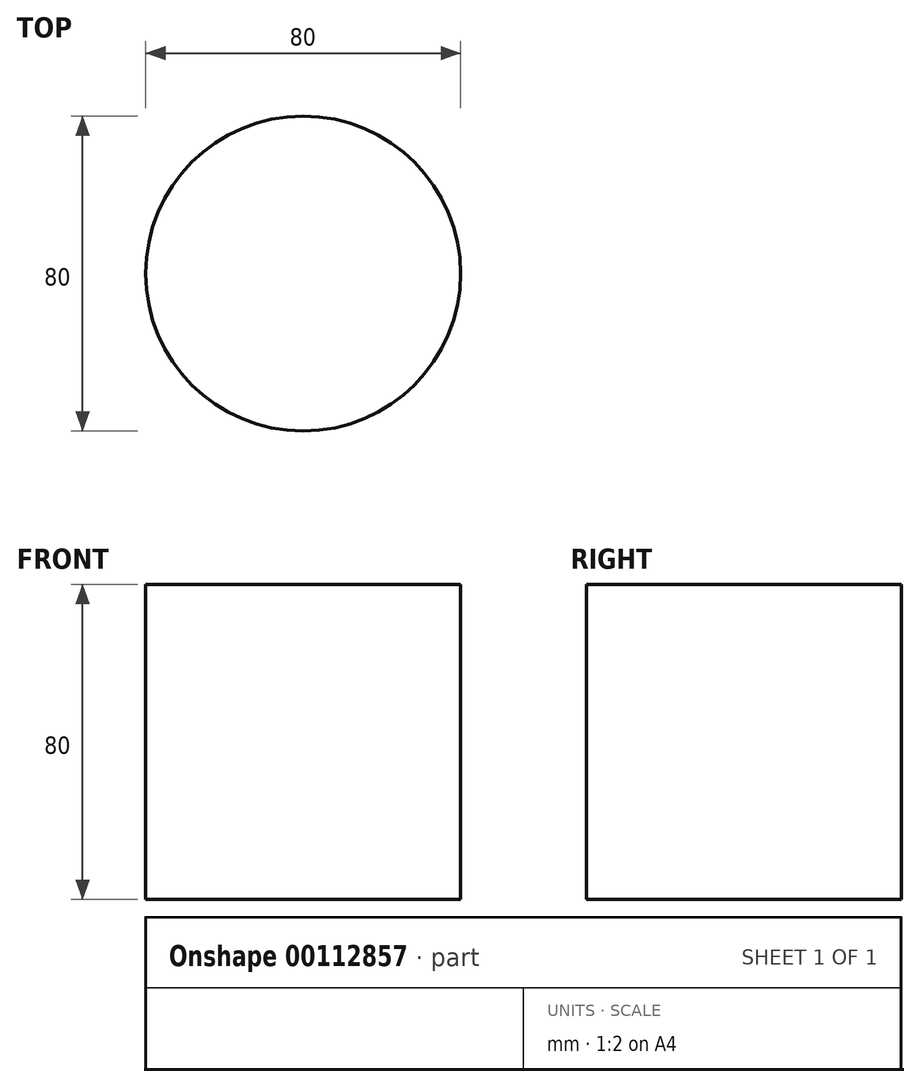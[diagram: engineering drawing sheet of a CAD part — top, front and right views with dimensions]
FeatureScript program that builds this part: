
annotation { "Feature Type Name" : "Feature", "Feature Type Description" : "" }
export const myFeature = defineFeature(function(context is Context, id is Id, definition is map)
    precondition{}
    {
        {
            var Q0;
            Q0=qCreatedBy(makeId("Top.planeOp"),FACE);
            var sketch = newSketch(context, id + "F0", { "sketchPlane" : qUnion([Q0])});
            skCircle(sketch, "E0", {"center": v(17.7, 0) * mm, "radius": 40 * mm});
            skSolve(sketch);
        }
        {
            var Q0;
            Q0=makeQuery(id+"F0.imprint","IMPRINT",FACE,{"disambiguationData":[TD([[makeQuery(id+"F0.imprint","IMPRINT",EDGE,{"derivedFrom":sQuery(id+"F0.wireOp",EDGE,"E0")}),1.0]])]});
            extrude(context, id + "F1", {"entities" : qUnion([Q0]), "depth" : 80 * mm});
        }
    });
